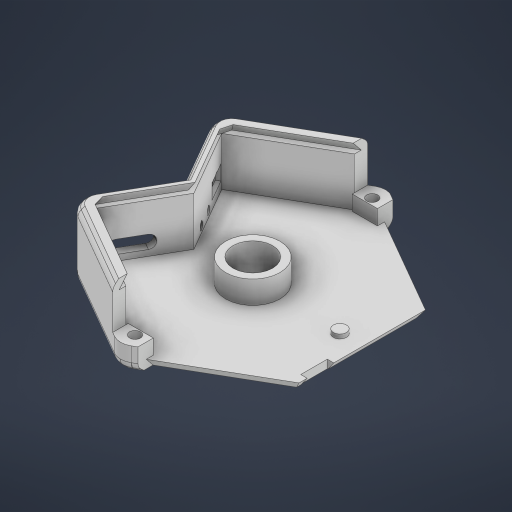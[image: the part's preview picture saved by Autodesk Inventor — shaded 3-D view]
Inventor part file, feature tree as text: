
AUTODESK INVENTOR PART (.ipt)
format: ipt  version: 2023 (Build 270158000, 158)  size: 781,312 bytes
history: native  units: in
note: dims shown in document units (in); Inventor stores cm internally (conversion verified against a paired STEP export)
features: extrude x28, sketch x17, move_body x8, direct_edit x6, draft x5, fillet x2, plane x1, chamfer x1
ambient origin geometry x8: Origin, YZ Plane, XZ Plane, XY Plane, X Axis, Y Axis, Z Axis, Center Point
bodies: Solid1 (feature_tree)
feature tree (68):
  sketch  "Sketch1"  dims[d0=1.939in d1=0.5157in]
  extrude  "Extrusion1"  Depth=0.5157in
  extrude  "Extrusion2"  Depth=0.4449in
  extrude  "Extrusion3"  Depth=0.0728in
  extrude  "Extrusion4"  Depth=0.0787in TaperAngle=0.0deg
  extrude  "Extrusion5"  Depth=0.6181in TaperAngle=0.0deg
  extrude  "Extrusion6"  Depth=0.1122in
  direct_edit  "Direct Edit1"
  extrude  "Extrusion9"  TaperAngle=0.0deg  [1 undecoded]
  extrude  "Extrusion10"  Depth=0.3307in TaperAngle=0.0deg
  extrude  "Extrusion11"  Depth=0.113in
  extrude  "Extrusion12"  Depth=0.2276in
  extrude  "Extrusion13"  TaperAngle=0.0deg  [1 undecoded]
  extrude  "Extrusion14"  Depth=0.1929in
  extrude  "Extrusion15"  Depth=0.185in
  extrude  "Extrusion16"  Depth=0.0689in
  direct_edit  "Direct Edit2"
  direct_edit  "Direct Edit3"
  sketch  "Sketch13"  dims[d21=0.176in d22=0.113in]
  extrude  "Extrusion17"  Depth=0.6871in
  sketch  "Sketch14"  dims[d23=0.1142in d24=0.2276in]
  extrude  "Extrusion19"  TaperAngle=0.0deg  [1 undecoded]
  sketch  "Sketch18"  dims[d25=0.1142in d26=0.0in d27=0.0in]
  extrude  "Extrusion26"  Depth=0.0787in TaperAngle=0.0deg
  extrude  "Extrusion27"  Depth=0.3937in TaperAngle=0.0deg
  sketch  "Sketch19"  dims[d33=0.0in d34=0.0in d35=-0.0728in d38=0.1929in]
  extrude  "Extrusion28"  TaperAngle=0.0deg  [1 undecoded]
  extrude  "Extrusion29"  Depth=0.3937in TaperAngle=0.0deg
  draft  "FaceDraft1"
  draft  "FaceDraft2"
  draft  "FaceDraft4"
  sketch  "Sketch20"  dims[d39=0.0591in d40=0.185in]
  extrude  "Extrusion30"  Depth=0.0787in TaperAngle=0.0deg
  extrude  "Extrusion31"  Depth=0.0787in
  extrude  "Extrusion32"  Depth=0.0787in
  direct_edit  "Direct Edit5"
  plane  "Work Plane1"
  sketch  "Sketch22"  dims[d43=0.0689in d44=0.6871in]
  extrude  "Extrusion37"  Depth=0.0787in TaperAngle=0.0deg
  extrude  "Extrusion38"  Depth=0.0787in
  extrude  "Extrusion39"  Depth=0.0787in TaperAngle=0.0deg
  extrude  "Extrusion40"  Depth=0.0787in TaperAngle=0.0deg
  extrude  "Extrusion42"  TaperAngle=0.0deg  [1 undecoded]
  draft  "FaceDraft5"
  fillet  "Fillet1"  Radius=0.2405in
  draft  "FaceDraft6"
  chamfer  "Chamfer5"  Distance=0.0787in
  fillet  "Fillet5"  [1 undecoded]
  direct_edit  "Direct Edit8"
  direct_edit  "Direct Edit9"
  sketch  "Sketch2"  dims[d2=0.374in d3=0.4449in]
  sketch  "Sketch3"  dims[d4=0.0295in d5=0.0728in]
  sketch  "Sketch4"  dims[d6=0.1378in d7=0.0787in d8=0.0in]
  sketch  "Sketch7"  dims[d9=0.2953in d10=0.0in d11=0.6181in d12=0.0in]
  sketch  "Sketch8"  dims[d13=0.2087in d14=0.1122in]
  sketch  "Sketch9"  dims[d15=0.1673in d16=0.0in d17=0.0in]
  sketch  "Sketch11"  dims[d18=0.0394in d19=0.3307in d20=0.0in]
  sketch  "Sketch21"  dims[d41=0.0591in d42=0.0689in]
  sketch  "Sketch23"  dims[d45=0.6871in d46=0.0in d47=0.0in]
  sketch  "Sketch24"  dims[d48=0.2953in d49=0.0787in d50=0.0in d51=0.3937in d52=0.0in d56=0.0in d57=0.0in d58=0.3937in d59=0.0in d60=0.3976in d61=0.0in d62=0.0315in d63=0.0787in d64=0.0689in d65=0.0in d66=0.0787in d67=0.0689in d68=0.0in d69=0.0in d70=0.0in d71=0.0787in d72=0.0in d73=0.0in d74=-0.0689in d78=0.2405in d80=0.0787in d81=0.0in d82=0.0in d85=0.2405in d86=0.0787in d87=0.0in d88=0.0in d116=30.0deg d117=0.0787in d118=0.0in d119=0.0in d120=0.3937in d121=0.0in d122=0.0787in d123=30.0deg d124=0.0in d125=0.0in d126=0.3937in d127=0.0in d128=0.2405in d129=-0.2405in d131=0.0in d132=0.0in d133=0.0787in d134=0.2405in d135=0.1614in d137=0.063in d138=0.0in d139=0.0709in d140=0.0in d141=0.0787in d142=0.0in d144=120.0deg d145=0.0in d146=0.0in d147=0.0157in d148=0.1575in d154=90.0deg d155=0.1921in d156=0.2953in d157=0.2028in d160=0.1354in d161=0.1535in d179=0.126in d180=0.8268in d181=0.0394in d182=0.0in d183=0.126in d184=0.126in d185=0.3937in d186=0.0in d199=0.0in d200=0.0in d201=0.1417in d202=0.0984in d204=0.0394in d205=0.0in d207=120.0deg d210=45.0deg d211=0.0in d212=0.0in d213=-0.2405in d214=-0.2405in d215=0.0492in d216=0.0787in d217=45.0deg d218=0.0787in d219=0.0157in d220=0.0118in d221=0.0in d222=0.0in d223=-0.0059in d224=0.1043in d226=0.0906in d228=0.0in d229=0.0in d230=0.0197in d231=0.0in d232=0.0in d233=-0.0197in d234=0.1535in d235=0.0079in d236=0.1535in d237=0.0906in d239=0.1043in d240=0.0079in d36=0.0344in d112=0.0197in d113=0.0344in d114=0.0197in d115=0.0344in d136=0.0344in d166=0.0197in d167=0.0344in d168=0.0197in d169=0.0344in d225=0.0197in d227=0.0197in]
  move_body  "Move1"
  move_body  "Move2"
  move_body  "Move3"
  move_body  "Move8"
  move_body  "Move9"
  move_body  "Move15"
  move_body  "Move16"
  move_body  "Move17"
note: 6 required parameter values undecoded (feature->parameter linkage not recoverable at this tier; creation-order binding heuristic only, values carry confidence <= 0.55)
